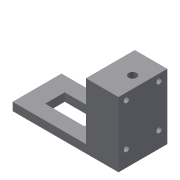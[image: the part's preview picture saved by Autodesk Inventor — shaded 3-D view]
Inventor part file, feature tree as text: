
AUTODESK INVENTOR PART (.ipt)
format: ipt  version: 2018 (Build 220112000, 112)  size: 102,400 bytes
history: native  units: mm
features: sketch x5, other x3
ambient origin geometry x8: Origin, YZ Plane, XZ Plane, XY Plane, X Axis, Y Axis, Z Axis, Center Point
bodies: Volumenkörper1 (feature_tree)
feature tree (8):
  other  "L-Halterung Servo.ipt"
  other  "Volumenkörper1::L-Halterung Servo.ipt"
  other  "Bezeichnung1"
  sketch  "Skizze1"  dims[d0=10.0mm]
  sketch  "Skizze2"
  sketch  "Skizze3"
  sketch  "Skizze4"
  sketch  "Skizze5"
